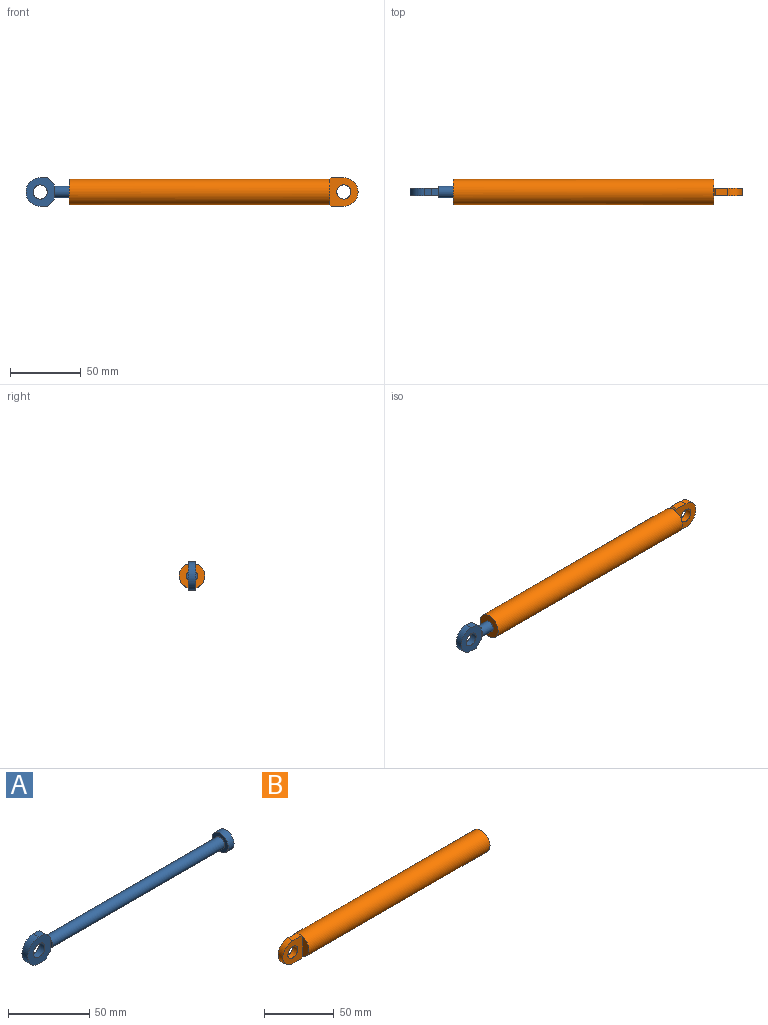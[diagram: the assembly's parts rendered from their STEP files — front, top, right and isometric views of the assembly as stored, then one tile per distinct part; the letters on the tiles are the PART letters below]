
ASSEMBLY  parts=2 mates=1
PART A: 16 faces, bbox 175x14x20 mm
  f0: plane 20x20mm, normal (0,1,0), area 253.5mm2, adj f3,f7,f8,f10,f11,f12,f13,f14
  f1: plane 6.25x1.5mm, normal (-1,0,0), area 6.5mm2, adj f2,f9
  f2: cylinder r=4mm len=150mm, axis (-1,0,0), area 3769.9mm2, adj f1,f3,f6,f7,f11
  f3: plane 6.25x1.5mm, normal (-1,0,0), area 6.5mm2, adj f0,f2
  f4: cylinder r=7mm len=14mm, axis (-1,0,0), area 219.9mm2, adj f5,f6
  f5: plane 14x14mm, normal (1,0,0), area 153.9mm2, adj f4
  f6: plane 14x14mm, normal (-1,0,0), area 103.7mm2, adj f2,f4
  f7: plane 5x1.88mm, normal (1,0,0), area 6.4mm2, adj f0,f2,f9,f15
  f8: plane 5x5mm, normal (0,0,-1), area 25mm2, adj f0,f9,f12,f14
  f9: plane 20x20mm, normal (0,-1,0), area 253.5mm2, adj f1,f7,f8,f10,f11,f12,f13,f14
  f10: plane 5x5mm, normal (0,0,1), area 25mm2, adj f0,f9,f12,f15
  f11: plane 5x1.88mm, normal (1,0,0), area 6.4mm2, adj f0,f2,f9,f14
  f12: cylinder r=10mm len=20mm, axis (0,-1,0), area 157.1mm2, adj f0,f8,f9,f10
  f13: cylinder r=5mm len=10mm, axis (0,-1,0), area 157.1mm2, adj f0,f9
  f14: plane 5x5mm, normal (0.71,0,-0.71), area 35.4mm2, adj f0,f8,f9,f11
  f15: plane 5x5mm, normal (0.71,0,0.71), area 35.4mm2, adj f0,f7,f9,f10
PART B: 20 faces, bbox 204x18x20 mm
  f0: plane 2.5x0.35mm, normal (1,0,0), area 0.3mm2, adj f2,f8,f19
  f1: plane 2.5x0.35mm, normal (1,0,0), area 0.3mm2, adj f8,f13,f18
  f2: plane 20x20mm, normal (0,1,0), area 277.5mm2, adj f0,f9,f12,f14,f15,f16,f17,f18
  f3: plane 17.29x6.5mm, normal (-1,0,0), area 82.8mm2, adj f8,f13
  f4: cylinder r=7mm len=180mm, axis (1,0,0), area 7916.8mm2, adj f5,f10
  f5: plane 14x14mm, normal (-1,0,0), area 103.7mm2, adj f4,f6
  f6: cylinder r=4mm len=8mm, axis (1,0,0), area 50.3mm2, adj f5,f7
  f7: plane 18x18mm, normal (1,0,0), area 204.2mm2, adj f6,f8
  f8: cylinder r=9mm len=184mm, axis (1,0,0), area 10405mm2, adj f0,f1,f3,f7,f9,f11,f15
  f9: plane 17.29x6.5mm, normal (-1,0,0), area 82.8mm2, adj f2,f8
  f10: plane 14x14mm, normal (1,0,0), area 153.9mm2, adj f4
  f11: plane 2.5x0.35mm, normal (1,0,0), area 0.3mm2, adj f8,f13,f19
  f12: plane 9x5mm, normal (0,0,-1), area 45mm2, adj f2,f13,f16,f18
  f13: plane 20x20mm, normal (0,-1,0), area 277.5mm2, adj f1,f3,f11,f12,f14,f16,f17,f18
  f14: plane 9x5mm, normal (0,0,1), area 45mm2, adj f2,f13,f16,f19
  f15: plane 2.5x0.35mm, normal (1,0,0), area 0.3mm2, adj f2,f8,f18
  f16: cylinder r=10mm len=20mm, axis (0,-1,0), area 157.1mm2, adj f2,f12,f13,f14
  f17: cylinder r=5mm len=10mm, axis (0,-1,0), area 157.1mm2, adj f2,f13
  f18: plane 5x1mm, normal (0.71,0,-0.71), area 7.1mm2, adj f1,f2,f12,f13,f15
  f19: plane 5x1mm, normal (0.71,0,0.71), area 7.1mm2, adj f0,f2,f11,f13,f14
PLACE A rot(axis=(1,0,0),0deg) t=(175.38,42.84,-59.55)mm
PLACE B rot(axis=(0,-1,0),180deg) t=(230.44,42.84,-59.55)mm fixed
MATE slider A.f4 <-> B.f4  axis (-1,0,0) through (252.88,42.84,-59.55)mm
